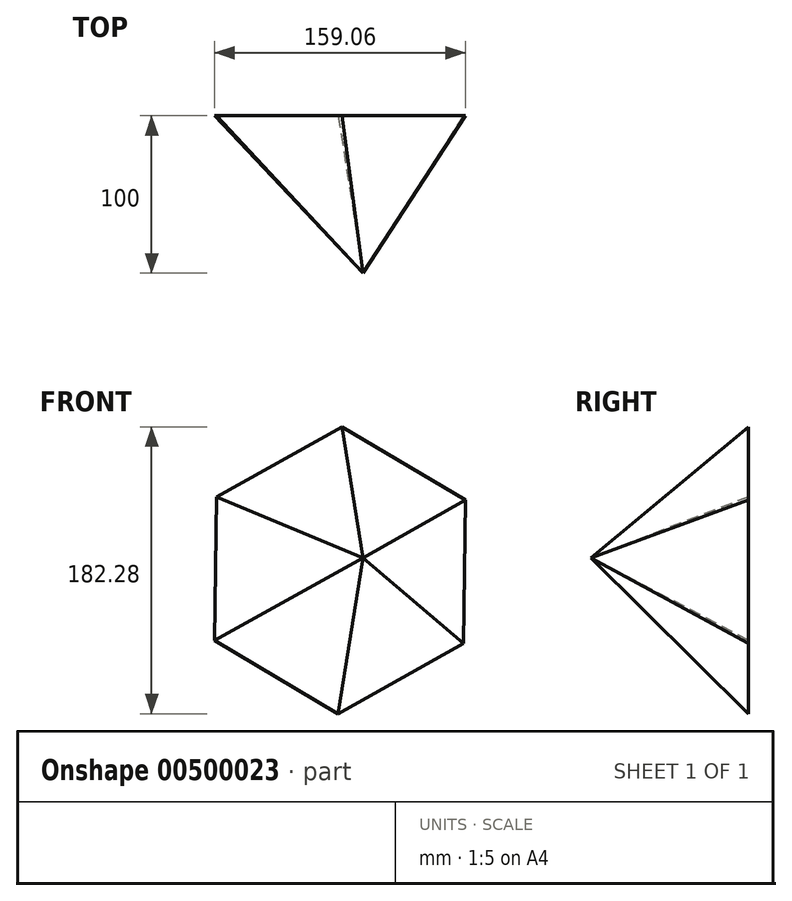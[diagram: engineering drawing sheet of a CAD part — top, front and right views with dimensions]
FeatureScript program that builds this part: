
annotation { "Feature Type Name" : "Feature", "Feature Type Description" : "" }
export const myFeature = defineFeature(function(context is Context, id is Id, definition is map)
    precondition{}
    {
        {
            var Q0;
            Q0=qCreatedBy(makeId("Front.planeOp"),FACE);
            var sketch = newSketch(context, id + "F0", { "sketchPlane" : qUnion([Q0])});
            skCircle(sketch, "E0.cCircle", {"center": v(0, 0) * mm, "radius": 91.14 * mm, "construction": true});
            skLineSegment(sketch, "E0.0", {"start": v(-78.32, 46.62) * mm, "end": v(1.21, 91.14) * mm});
            skLineSegment(sketch, "E0.1", {"start": v(1.21, 91.14) * mm, "end": v(79.53, 44.52) * mm});
            skLineSegment(sketch, "E0.2", {"start": v(79.53, 44.52) * mm, "end": v(78.32, -46.62) * mm});
            skLineSegment(sketch, "E0.3", {"start": v(78.32, -46.62) * mm, "end": v(-1.21, -91.14) * mm});
            skLineSegment(sketch, "E0.4", {"start": v(-1.21, -91.14) * mm, "end": v(-79.53, -44.52) * mm});
            skLineSegment(sketch, "E0.5", {"start": v(-79.53, -44.52) * mm, "end": v(-78.32, 46.62) * mm});
            skSolve(sketch);
        }
        {
            var Q0;
            Q0=qCreatedBy(makeId("Front.planeOp"),FACE);
            cPlane(context, id + "F1", {"entities" : qUnion([Q0]), "cplaneType" : CPlaneType.OFFSET, "offset" : 100 * mm, "width" : 150 * mm, "height" : 150 * mm});
        }
        {
            var Q0;
            Q0=qCreatedBy(id+"F1.planeOp",FACE);
            var sketch = newSketch(context, id + "F2", { "sketchPlane" : qUnion([Q0])});
            skPoint(sketch, "E1", {"position": v(14.66, 7.95) * mm});
            skSolve(sketch);
        }
        {
            var Q0;
            Q0=makeQuery(id+"F0.imprint","IMPRINT",FACE,{"disambiguationData":[TD([[makeQuery(id+"F0.imprint","IMPRINT",EDGE,{"derivedFrom":sQuery(id+"F0.wireOp",EDGE,"E0.0")}),-1.0]])]});
            var Q1;
            Q1=sQuery(id+"F2.wireOp",VERTEX,"E1");
            loft(context, id + "F3", {"sheetProfilesArray" : [{ "sheetProfileEntities" : qUnion([Q0]) }, { "sheetProfileEntities" : qUnion([Q1]) }]});
        }
    });
